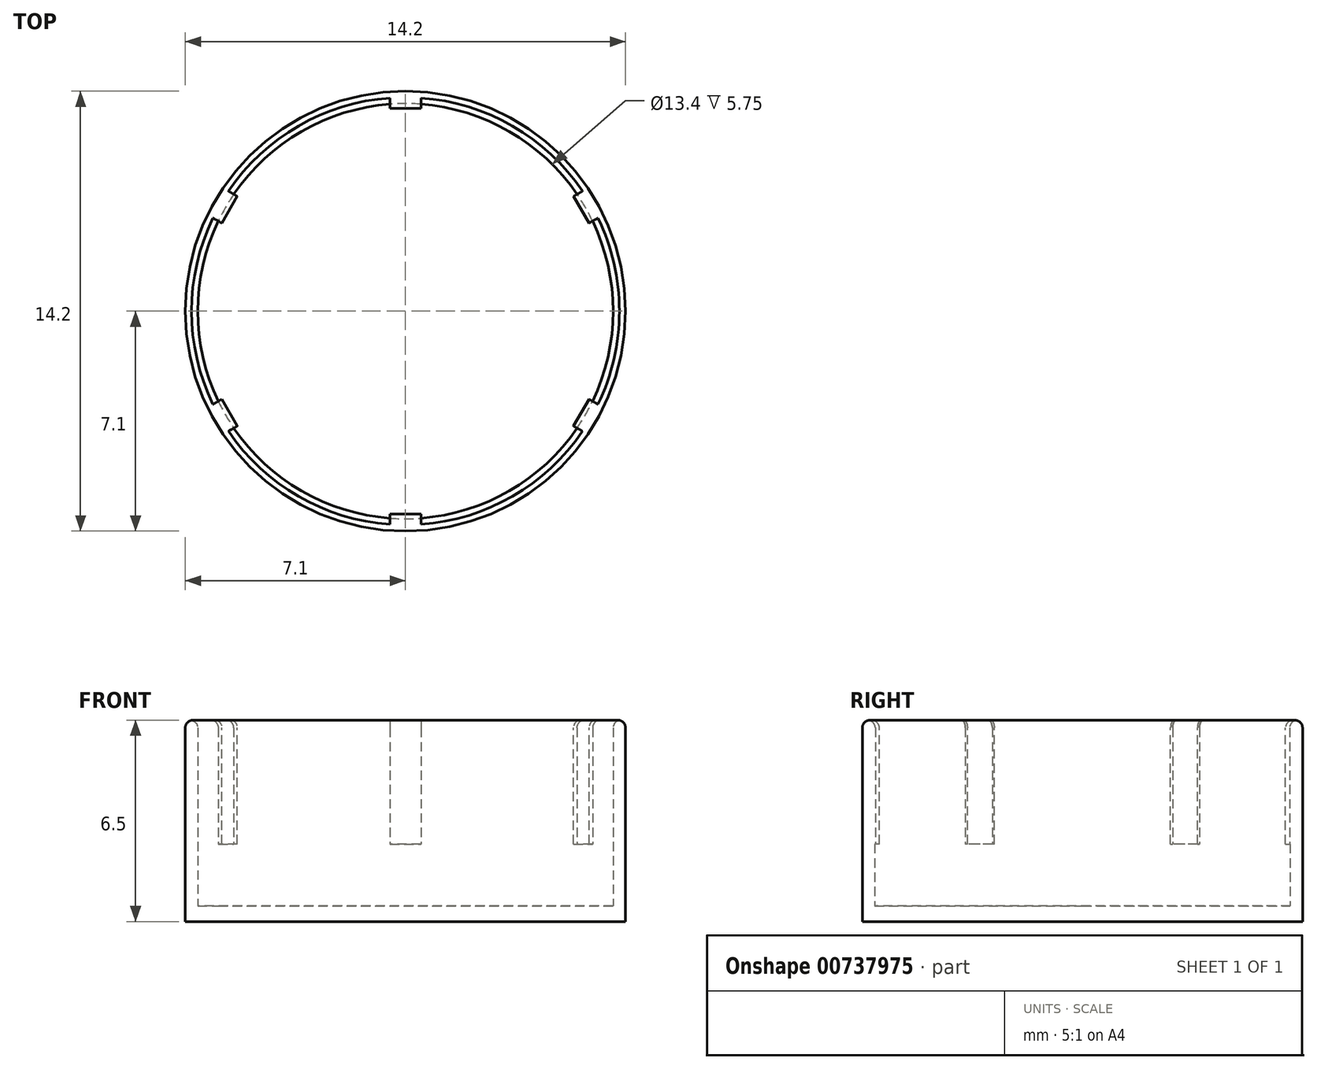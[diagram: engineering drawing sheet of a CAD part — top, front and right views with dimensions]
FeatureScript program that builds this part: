
annotation { "Feature Type Name" : "Feature", "Feature Type Description" : "" }
export const myFeature = defineFeature(function(context is Context, id is Id, definition is map)
    precondition{}
    {
        {
            var Q0;
            Q0=qCreatedBy(makeId("Top.planeOp"),FACE);
            var sketch = newSketch(context, id + "F0", { "sketchPlane" : qUnion([Q0])});
            skCircle(sketch, "E0", {"center": v(0, 0) * mm, "radius": 7.1 * mm});
            skSolve(sketch);
        }
        {
            var Q0;
            Q0=makeQuery(id+"F0.imprint","IMPRINT",FACE,{"disambiguationData":[TD([[makeQuery(id+"F0.imprint","IMPRINT",EDGE,{"derivedFrom":sQuery(id+"F0.wireOp",EDGE,"E0")}),1.0]])]});
            extrude(context, id + "F1", {"entities" : qUnion([Q0]), "depth" : 0.5 * mm, "offsetDistance" : 25 * mm});
        }
        {
            var Q0;
            Q0=makeQuery(id+"F1.opExtrude","CAP_FACE",FACE,{"disambiguationData":[OSD([sQuery(id+"F0.wireOp",EDGE,"E0")])],"isStart":false});
            var sketch = newSketch(context, id + "F2", { "sketchPlane" : qUnion([Q0])});
            skCircle(sketch, "E1", {"center": v(0, 0) * mm, "radius": 6.7 * mm});
            skCircle(sketch, "E2", {"center": v(0, 0) * mm, "radius": 7.1 * mm});
            skSolve(sketch);
        }
        {
            var Q0;
            Q0 = qSketchRegion(id + "F2", true);
            extrude(context, id + "F3", {"entities" : qUnion([Q0]), "operationType" : NewBodyOperationType.ADD, "depth" : 6 * mm, "offsetDistance" : 25 * mm});
        }
        {
            var Q0;
            Q0=makeQuery(id+"F3.opExtrude","CAP_FACE",FACE,{"disambiguationData":[OSD([sQuery(id+"F2.wireOp",EDGE,"E1"),sQuery(id+"F2.wireOp",EDGE,"E2")])],"isStart":false});
            var sketch = newSketch(context, id + "F4", { "sketchPlane" : qUnion([Q0])});
            skLineSegment(sketch, "E3.bottom", {"start": v(0.5, 6.55) * mm, "end": v(-0.5, 6.55) * mm});
            skLineSegment(sketch, "E3.top", {"start": v(0.5, 6.85) * mm, "end": v(-0.5, 6.85) * mm});
            skLineSegment(sketch, "E3.left", {"start": v(0.5, 6.55) * mm, "end": v(0.5, 6.85) * mm});
            skLineSegment(sketch, "E3.right", {"start": v(-0.5, 6.55) * mm, "end": v(-0.5, 6.85) * mm});
            skPoint(sketch, "E3.middle", {"position": v(0, 6.7) * mm});
            skLineSegment(sketch, "E4.1.0", {"start": v(-5.42, 3.7) * mm, "end": v(-5.92, 2.84) * mm});
            skLineSegment(sketch, "E4.1.1", {"start": v(-5.42, 3.7) * mm, "end": v(-5.68, 3.86) * mm});
            skLineSegment(sketch, "E4.1.2", {"start": v(-5.68, 3.86) * mm, "end": v(-6.18, 3) * mm});
            skPoint(sketch, "E4.1.3", {"position": v(-5.8, 3.35) * mm});
            skLineSegment(sketch, "E4.1.4", {"start": v(-5.92, 2.84) * mm, "end": v(-6.18, 3) * mm});
            skLineSegment(sketch, "E4.2.0", {"start": v(-5.92, -2.84) * mm, "end": v(-5.42, -3.7) * mm});
            skLineSegment(sketch, "E4.2.1", {"start": v(-5.92, -2.84) * mm, "end": v(-6.18, -3) * mm});
            skLineSegment(sketch, "E4.2.2", {"start": v(-6.18, -3) * mm, "end": v(-5.68, -3.86) * mm});
            skPoint(sketch, "E4.2.3", {"position": v(-5.8, -3.35) * mm});
            skLineSegment(sketch, "E4.2.4", {"start": v(-5.42, -3.7) * mm, "end": v(-5.68, -3.86) * mm});
            skLineSegment(sketch, "E4.3.0", {"start": v(-0.5, -6.55) * mm, "end": v(0.5, -6.55) * mm});
            skLineSegment(sketch, "E4.3.1", {"start": v(-0.5, -6.55) * mm, "end": v(-0.5, -6.85) * mm});
            skLineSegment(sketch, "E4.3.2", {"start": v(-0.5, -6.85) * mm, "end": v(0.5, -6.85) * mm});
            skPoint(sketch, "E4.3.3", {"position": v(0, -6.7) * mm});
            skLineSegment(sketch, "E4.3.4", {"start": v(0.5, -6.55) * mm, "end": v(0.5, -6.85) * mm});
            skLineSegment(sketch, "E4.4.0", {"start": v(5.42, -3.7) * mm, "end": v(5.92, -2.84) * mm});
            skLineSegment(sketch, "E4.4.1", {"start": v(5.42, -3.7) * mm, "end": v(5.68, -3.86) * mm});
            skLineSegment(sketch, "E4.4.2", {"start": v(5.68, -3.86) * mm, "end": v(6.18, -3) * mm});
            skPoint(sketch, "E4.4.3", {"position": v(5.8, -3.35) * mm});
            skLineSegment(sketch, "E4.4.4", {"start": v(5.92, -2.84) * mm, "end": v(6.18, -3) * mm});
            skLineSegment(sketch, "E4.5.0", {"start": v(5.92, 2.84) * mm, "end": v(5.42, 3.7) * mm});
            skLineSegment(sketch, "E4.5.1", {"start": v(5.92, 2.84) * mm, "end": v(6.18, 3) * mm});
            skLineSegment(sketch, "E4.5.2", {"start": v(6.18, 3) * mm, "end": v(5.68, 3.86) * mm});
            skPoint(sketch, "E4.5.3", {"position": v(5.8, 3.35) * mm});
            skLineSegment(sketch, "E4.5.4", {"start": v(5.42, 3.7) * mm, "end": v(5.68, 3.86) * mm});
            skPoint(sketch, "E4.center", {"position": v(0, 0) * mm});
            skSolve(sketch);
        }
        {
            var Q0;
            Q0 = qSketchRegion(id + "F4", true);
            extrude(context, id + "F5", {"entities" : qUnion([Q0]), "operationType" : NewBodyOperationType.ADD, "oppositeDirection" : true, "depth" : 4 * mm, "offsetDistance" : 25 * mm});
        }
        {
            var Q0;
            Q0=makeQuery(id+"F3.opExtrude","CAP_EDGE",EDGE,{"disambiguationData":[OSD([sQuery(id+"F2.wireOp",EDGE,"E2")])],"isStart":false});
            fillet(context, id + "F6", {"entities" : qUnion([Q0]), "radius" : 0.25 * mm, "tangentPropagation" : true, "allowEdgeOverflow" : false});
        }
        {
            var Q0;
            {var subQ0=sQuery(id+"F2.wireOp",EDGE,"E1");var subQ2=sQuery(id+"F4.wireOp",EDGE,"E4.2.4");Q0=makeQuery(id+"F5.boolean.opBoolean","SPLIT",EDGE,{"disambiguationData":[TD([makeQuery(id+"F5.opExtrude","SWEPT_FACE",FACE,{"disambiguationData":[OSD([subQ2])]})])],"derivedFrom":makeQuery(id+"F3.opExtrude","CAP_EDGE",EDGE,{"disambiguationData":[OSD([subQ0])],"isStart":false})});}
            var Q1;
            {var subQ0=sQuery(id+"F4.wireOp",EDGE,"E4.1.4");var subQ1=sQuery(id+"F2.wireOp",EDGE,"E1");Q1=makeQuery(id+"F5.boolean.opBoolean","SPLIT",EDGE,{"disambiguationData":[TD([makeQuery(id+"F5.opExtrude","SWEPT_FACE",FACE,{"disambiguationData":[OSD([subQ0])]})])],"derivedFrom":makeQuery(id+"F3.opExtrude","CAP_EDGE",EDGE,{"disambiguationData":[OSD([subQ1])],"isStart":false})});}
            var Q2;
            {var subQ0=sQuery(id+"F4.wireOp",EDGE,"E3.right");var subQ1=sQuery(id+"F2.wireOp",EDGE,"E1");Q2=makeQuery(id+"F5.boolean.opBoolean","SPLIT",EDGE,{"disambiguationData":[TD([makeQuery(id+"F5.opExtrude","SWEPT_FACE",FACE,{"disambiguationData":[OSD([subQ0])]})])],"derivedFrom":makeQuery(id+"F3.opExtrude","CAP_EDGE",EDGE,{"disambiguationData":[OSD([subQ1])],"isStart":false})});}
            var Q3;
            {var subQ0=sQuery(id+"F4.wireOp",EDGE,"E3.left");var subQ1=sQuery(id+"F2.wireOp",EDGE,"E1");Q3=makeQuery(id+"F5.boolean.opBoolean","SPLIT",EDGE,{"disambiguationData":[TD([makeQuery(id+"F5.opExtrude","SWEPT_FACE",FACE,{"disambiguationData":[OSD([subQ0])]})])],"derivedFrom":makeQuery(id+"F3.opExtrude","CAP_EDGE",EDGE,{"disambiguationData":[OSD([subQ1])],"isStart":false})});}
            var Q4;
            {var subQ0=sQuery(id+"F4.wireOp",EDGE,"E4.4.4");var subQ1=sQuery(id+"F2.wireOp",EDGE,"E1");Q4=makeQuery(id+"F5.boolean.opBoolean","SPLIT",EDGE,{"disambiguationData":[TD([makeQuery(id+"F5.opExtrude","SWEPT_FACE",FACE,{"disambiguationData":[OSD([subQ0])]})])],"derivedFrom":makeQuery(id+"F3.opExtrude","CAP_EDGE",EDGE,{"disambiguationData":[OSD([subQ1])],"isStart":false})});}
            var Q5;
            {var subQ0=sQuery(id+"F2.wireOp",EDGE,"E1");var subQ1=sQuery(id+"F4.wireOp",EDGE,"E4.3.4");Q5=makeQuery(id+"F5.boolean.opBoolean","SPLIT",EDGE,{"disambiguationData":[TD([makeQuery(id+"F5.opExtrude","SWEPT_FACE",FACE,{"disambiguationData":[OSD([subQ1])]})])],"derivedFrom":makeQuery(id+"F3.opExtrude","CAP_EDGE",EDGE,{"disambiguationData":[OSD([subQ0])],"isStart":false})});}
            fillet(context, id + "F7", {"entities" : qUnion([Q0, Q1, Q2, Q3, Q4, Q5]), "radius" : 0.25 * mm, "tangentPropagation" : true, "allowEdgeOverflow" : false});
        }
        {
            var Q0;
            Q0=makeQuery(id+"F5.opExtrude","CAP_EDGE",EDGE,{"disambiguationData":[OSD([sQuery(id+"F4.wireOp",EDGE,"E4.1.0")])],"isStart":true});
            var Q1;
            Q1=makeQuery(id+"F5.opExtrude","CAP_EDGE",EDGE,{"disambiguationData":[OSD([sQuery(id+"F4.wireOp",EDGE,"E3.bottom")])],"isStart":true});
            var Q2;
            Q2=makeQuery(id+"F5.opExtrude","CAP_EDGE",EDGE,{"disambiguationData":[OSD([sQuery(id+"F4.wireOp",EDGE,"E4.5.0")])],"isStart":true});
            var Q3;
            Q3=makeQuery(id+"F5.opExtrude","CAP_EDGE",EDGE,{"disambiguationData":[OSD([sQuery(id+"F4.wireOp",EDGE,"E4.4.0")])],"isStart":true});
            var Q4;
            Q4=makeQuery(id+"F5.opExtrude","CAP_EDGE",EDGE,{"disambiguationData":[OSD([sQuery(id+"F4.wireOp",EDGE,"E4.3.0")])],"isStart":true});
            var Q5;
            Q5=makeQuery(id+"F5.opExtrude","CAP_EDGE",EDGE,{"disambiguationData":[OSD([sQuery(id+"F4.wireOp",EDGE,"E4.2.0")])],"isStart":true});
            fillet(context, id + "F8", {"entities" : qUnion([Q0, Q1, Q2, Q3, Q4, Q5]), "radius" : 0.25 * mm, "tangentPropagation" : true, "allowEdgeOverflow" : false});
        }
    });
